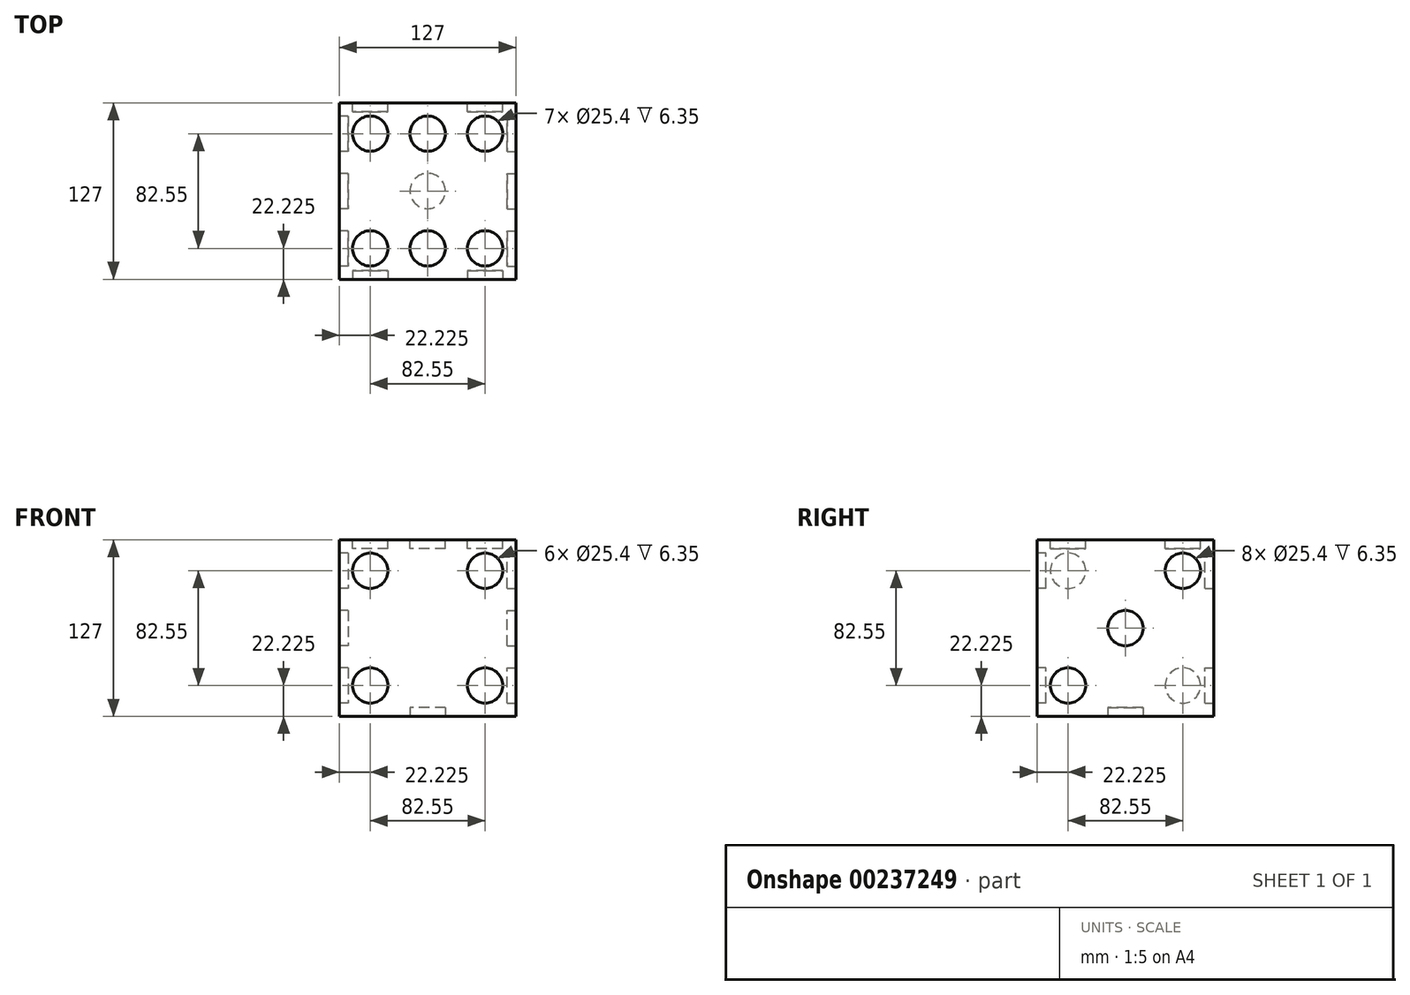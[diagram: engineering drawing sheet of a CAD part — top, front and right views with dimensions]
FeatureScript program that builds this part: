
annotation { "Feature Type Name" : "Feature", "Feature Type Description" : "" }
export const myFeature = defineFeature(function(context is Context, id is Id, definition is map)
    precondition{}
    {
        {
            var Q0;
            Q0=qCreatedBy(makeId("Front.planeOp"),FACE);
            var sketch = newSketch(context, id + "F0", { "sketchPlane" : qUnion([Q0])});
            skLineSegment(sketch, "E0.bottom", {"start": v(0, 0) * mm, "end": v(127, 0) * mm});
            skLineSegment(sketch, "E0.top", {"start": v(0, 127) * mm, "end": v(127, 127) * mm});
            skLineSegment(sketch, "E0.left", {"start": v(0, 0) * mm, "end": v(0, 127) * mm});
            skLineSegment(sketch, "E0.right", {"start": v(127, 0) * mm, "end": v(127, 127) * mm});
            skSolve(sketch);
        }
        {
            var Q0;
            Q0 = qSketchRegion(id + "F0", true);
            extrude(context, id + "F1", {"entities" : qUnion([Q0]), "depth" : 127 * mm});
        }
        {
            var Q0;
            Q0=qCreatedBy(makeId("Top.planeOp"),FACE);
            var sketch = newSketch(context, id + "F2", { "sketchPlane" : qUnion([Q0])});
            skCircle(sketch, "E1", {"center": v(63.5, -63.5) * mm, "radius": 12.7 * mm});
            skSolve(sketch);
        }
        {
            var Q0;
            Q0=makeQuery(id+"F2.imprint","IMPRINT",FACE,{"disambiguationData":[TD([[makeQuery(id+"F2.imprint","IMPRINT",EDGE,{"derivedFrom":sQuery(id+"F2.wireOp",EDGE,"E1")}),1.0]])]});
            extrude(context, id + "F3", {"entities" : qUnion([Q0]), "operationType" : NewBodyOperationType.REMOVE, "depth" : 6.35 * mm});
        }
        {
            var Q0;
            Q0=makeQuery(id+"F0.imprint","IMPRINT",FACE,{"disambiguationData":[TD([[makeQuery(id+"F0.imprint","IMPRINT",EDGE,{"derivedFrom":sQuery(id+"F0.wireOp",EDGE,"E0.bottom")}),1.0]])]});
            var sketch = newSketch(context, id + "F4", { "sketchPlane" : qUnion([Q0])});
            skCircle(sketch, "E2", {"center": v(104.77, 22.23) * mm, "radius": 12.7 * mm});
            skCircle(sketch, "E3", {"center": v(22.23, 104.78) * mm, "radius": 12.7 * mm});
            skSolve(sketch);
        }
        {
            var Q0;
            Q0 = qSketchRegion(id + "F4", true);
            extrude(context, id + "F5", {"entities" : qUnion([Q0]), "operationType" : NewBodyOperationType.REMOVE, "depth" : 6.35 * mm});
        }
        {
            var Q0;
            Q0=makeQuery(id+"F1.opExtrude","SWEPT_FACE",FACE,{"disambiguationData":[OSD([sQuery(id+"F0.wireOp",EDGE,"E0.right")])]});
            var sketch = newSketch(context, id + "F6", { "sketchPlane" : qUnion([Q0])});
            skCircle(sketch, "E4", {"center": v(-22.23, 104.78) * mm, "radius": 12.7 * mm});
            skCircle(sketch, "E5", {"center": v(-63.5, 63.5) * mm, "radius": 12.7 * mm});
            skCircle(sketch, "E6", {"center": v(-104.78, 22.22) * mm, "radius": 12.7 * mm});
            skSolve(sketch);
        }
        {
            var Q0;
            Q0 = qSketchRegion(id + "F6", true);
            extrude(context, id + "F7", {"entities" : qUnion([Q0]), "operationType" : NewBodyOperationType.REMOVE, "oppositeDirection" : true, "depth" : 6.35 * mm});
        }
        {
            var Q0;
            Q0=makeQuery(id+"F1.opExtrude","CAP_FACE",FACE,{"disambiguationData":[OSD([sQuery(id+"F0.wireOp",EDGE,"E0.bottom"),sQuery(id+"F0.wireOp",EDGE,"E0.top"),sQuery(id+"F0.wireOp",EDGE,"E0.left"),sQuery(id+"F0.wireOp",EDGE,"E0.right")])],"isStart":false});
            var sketch = newSketch(context, id + "F8", { "sketchPlane" : qUnion([Q0])});
            skCircle(sketch, "E7", {"center": v(104.77, 104.78) * mm, "radius": 12.7 * mm});
            skCircle(sketch, "E8", {"center": v(104.77, 22.23) * mm, "radius": 12.7 * mm});
            skCircle(sketch, "E9", {"center": v(22.23, 22.23) * mm, "radius": 12.7 * mm});
            skCircle(sketch, "E10", {"center": v(22.23, 104.78) * mm, "radius": 12.7 * mm});
            skSolve(sketch);
        }
        {
            var Q0;
            Q0 = qSketchRegion(id + "F8", true);
            extrude(context, id + "F9", {"entities" : qUnion([Q0]), "operationType" : NewBodyOperationType.REMOVE, "oppositeDirection" : true, "depth" : 6.35 * mm});
        }
        {
            var Q0;
            Q0=makeQuery(id+"F1.opExtrude","SWEPT_FACE",FACE,{"disambiguationData":[OSD([sQuery(id+"F0.wireOp",EDGE,"E0.left")])]});
            var sketch = newSketch(context, id + "F10", { "sketchPlane" : qUnion([Q0])});
            skCircle(sketch, "E11", {"center": v(104.78, 22.23) * mm, "radius": 12.7 * mm});
            skCircle(sketch, "E12", {"center": v(22.23, 22.23) * mm, "radius": 12.7 * mm});
            skCircle(sketch, "E13", {"center": v(63.5, 63.5) * mm, "radius": 12.7 * mm});
            skCircle(sketch, "E14", {"center": v(104.78, 104.78) * mm, "radius": 12.7 * mm});
            skCircle(sketch, "E15", {"center": v(22.23, 104.78) * mm, "radius": 12.7 * mm});
            skSolve(sketch);
        }
        {
            var Q0;
            Q0 = qSketchRegion(id + "F10", true);
            extrude(context, id + "F11", {"entities" : qUnion([Q0]), "operationType" : NewBodyOperationType.REMOVE, "oppositeDirection" : true, "depth" : 6.35 * mm});
        }
        {
            var Q0;
            Q0=makeQuery(id+"F1.opExtrude","SWEPT_FACE",FACE,{"disambiguationData":[OSD([sQuery(id+"F0.wireOp",EDGE,"E0.top")])]});
            var sketch = newSketch(context, id + "F12", { "sketchPlane" : qUnion([Q0])});
            skCircle(sketch, "E16", {"center": v(22.23, -104.78) * mm, "radius": 12.7 * mm});
            skCircle(sketch, "E17", {"center": v(63.5, -104.78) * mm, "radius": 12.7 * mm});
            skCircle(sketch, "E18", {"center": v(104.77, -104.78) * mm, "radius": 12.7 * mm});
            skCircle(sketch, "E19", {"center": v(104.77, -22.22) * mm, "radius": 12.7 * mm});
            skCircle(sketch, "E20", {"center": v(63.5, -22.23) * mm, "radius": 12.7 * mm});
            skCircle(sketch, "E21", {"center": v(22.23, -22.23) * mm, "radius": 12.7 * mm});
            skSolve(sketch);
        }
        {
            var Q0;
            Q0 = qSketchRegion(id + "F12", true);
            extrude(context, id + "F13", {"entities" : qUnion([Q0]), "operationType" : NewBodyOperationType.REMOVE, "oppositeDirection" : true, "depth" : 6.35 * mm});
        }
    });
